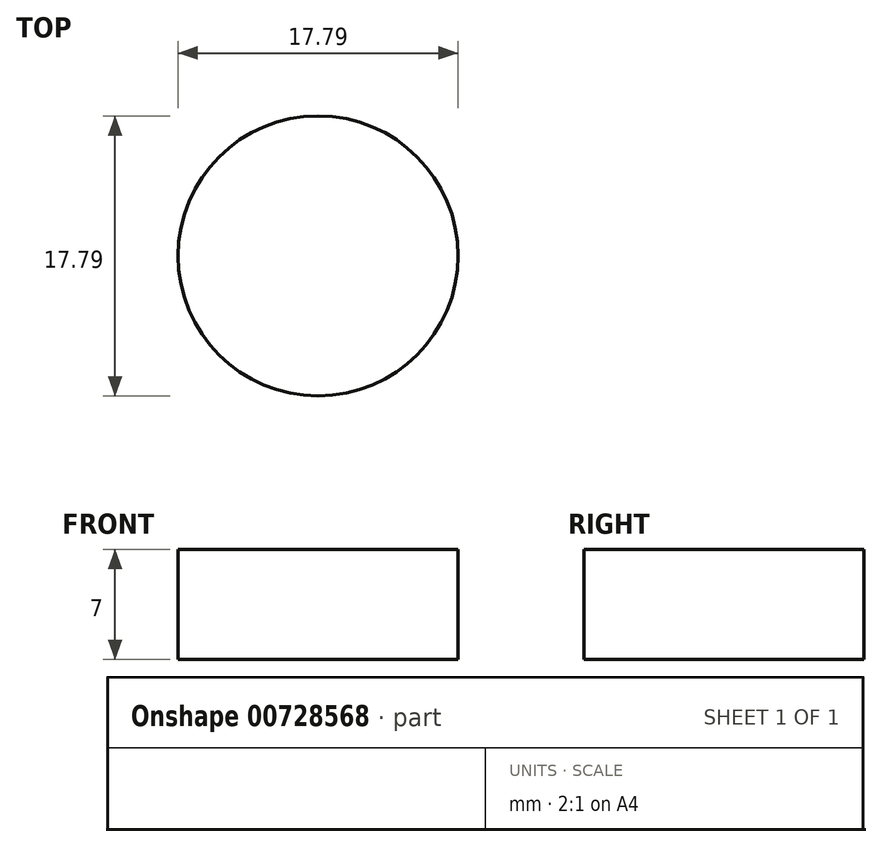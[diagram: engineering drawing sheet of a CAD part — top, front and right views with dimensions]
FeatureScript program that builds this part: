
annotation { "Feature Type Name" : "Feature", "Feature Type Description" : "" }
export const myFeature = defineFeature(function(context is Context, id is Id, definition is map)
    precondition{}
    {
        {
            var Q0;
            Q0=qCreatedBy(makeId("Top.planeOp"),FACE);
            var sketch = newSketch(context, id + "F0", { "sketchPlane" : qUnion([Q0])});
            skLineSegment(sketch, "E0", {"start": v(-50.24, 31.3) * mm, "end": v(-50.24, 14.2) * mm});
            skLineSegment(sketch, "E1", {"start": v(-50.24, 31.3) * mm, "end": v(-38.94, 16.64) * mm});
            skLineSegment(sketch, "E2", {"start": v(-38.94, 16.64) * mm, "end": v(-38.94, 31.3) * mm});
            skCircle(sketch, "E3", {"center": v(-26.42, 25.2) * mm, "radius": 8.9 * mm});
            skSolve(sketch);
        }
        {
            var Q0;
            Q0 = qSketchRegion(id + "F0", true);
            extrude(context, id + "F1", {"entities" : qUnion([Q0]), "depth" : 7 * mm, "offsetDistance" : 25 * mm});
        }
    });
